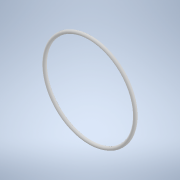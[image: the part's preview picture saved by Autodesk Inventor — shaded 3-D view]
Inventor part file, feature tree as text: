
AUTODESK INVENTOR PART (.ipt)
format: ipt  version: 2020.2 (Build 242310000, 310)  size: 115,712 bytes
history: native  units: mm
features: revolve x1, sketch x1
ambient origin geometry x8: Origin, YZ Plane, XZ Plane, XY Plane, X Axis, Y Axis, Z Axis, Center Point
bodies: Volumenkörper1 (feature_tree)
feature tree (2):
  revolve  "Umdrehung1"
  sketch  "Skizze1"  dims[d2=90.0deg d3=27.5mm]
